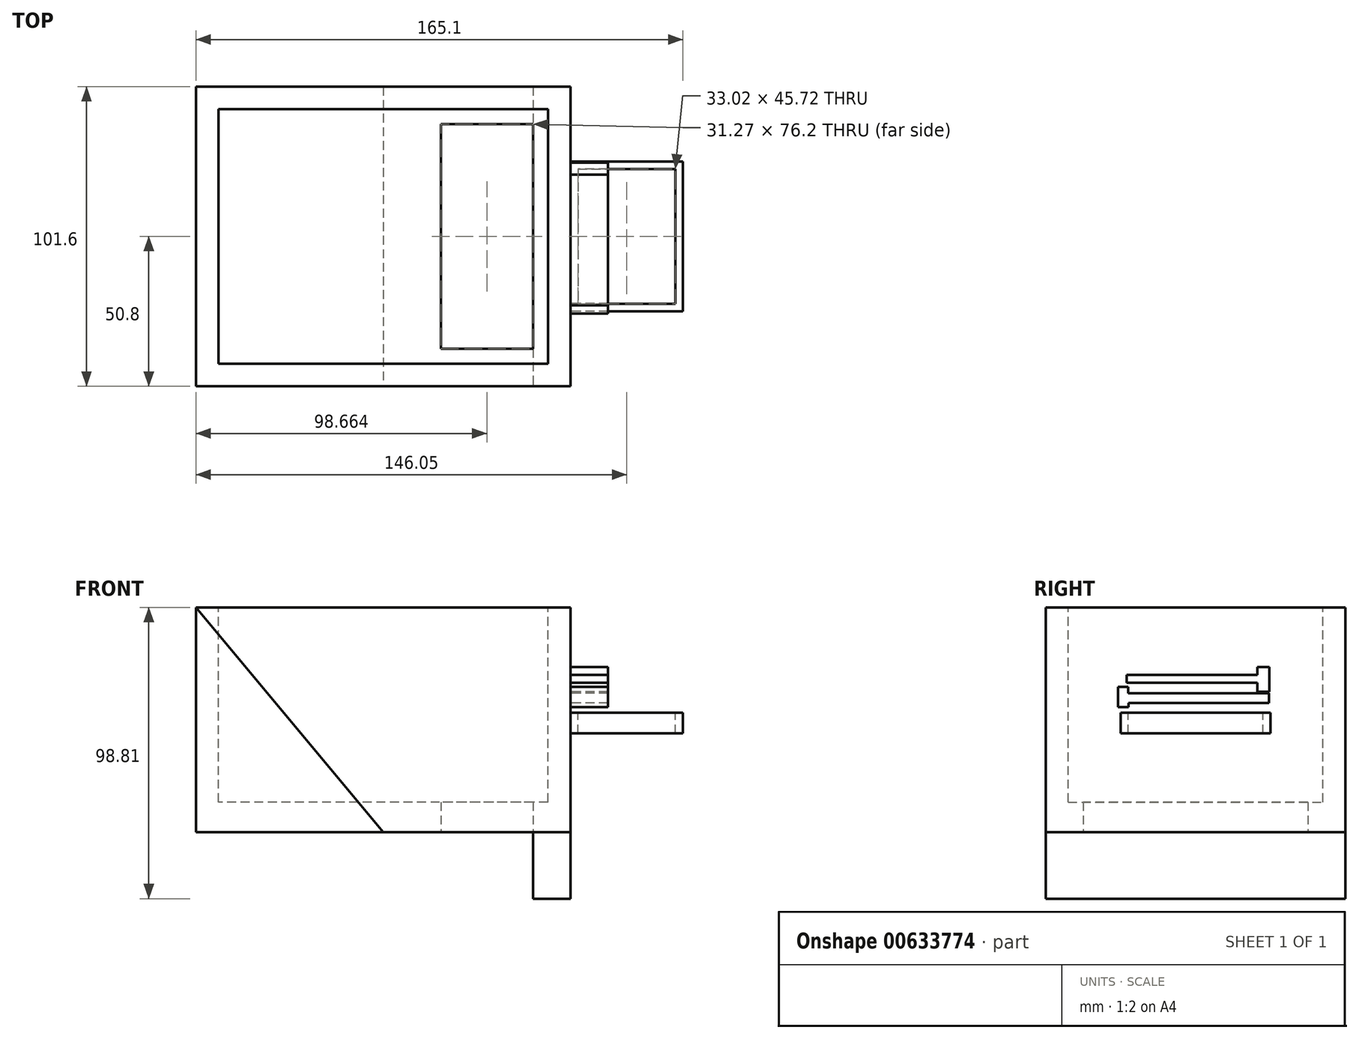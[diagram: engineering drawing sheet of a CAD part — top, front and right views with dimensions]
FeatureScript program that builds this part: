
annotation { "Feature Type Name" : "Feature", "Feature Type Description" : "" }
export const myFeature = defineFeature(function(context is Context, id is Id, definition is map)
    precondition{}
    {
        {
            var Q0;
            Q0=qCreatedBy(makeId("Front.planeOp"),FACE);
            var sketch = newSketch(context, id + "F0", { "sketchPlane" : qUnion([Q0])});
            skLineSegment(sketch, "E0", {"start": v(0, 0) * mm, "end": v(0, 76.2) * mm});
            skLineSegment(sketch, "E1", {"start": v(0, 76.2) * mm, "end": v(127, 76.2) * mm});
            skLineSegment(sketch, "E2", {"start": v(127, 76.2) * mm, "end": v(127, 0) * mm});
            skLineSegment(sketch, "E3", {"start": v(127, 0) * mm, "end": v(0, 0) * mm});
            skSolve(sketch);
        }
        {
            var Q0;
            Q0=makeQuery(id+"F0.imprint","IMPRINT",FACE,{"disambiguationData":[TD([[makeQuery(id+"F0.imprint","IMPRINT",EDGE,{"derivedFrom":sQuery(id+"F0.wireOp",EDGE,"E0")}),-1.0]])]});
            extrude(context, id + "F1", {"entities" : qUnion([Q0]), "oppositeDirection" : true, "depth" : 101.6 * mm, "offsetDistance" : 25.4 * mm});
        }
        {
            var Q0;
            Q0=makeQuery(id+"F1.opExtrude","SWEPT_FACE",FACE,{"disambiguationData":[OSD([sQuery(id+"F0.wireOp",EDGE,"E1")])]});
            var sketch = newSketch(context, id + "F2", { "sketchPlane" : qUnion([Q0])});
            skLineSegment(sketch, "E4", {"start": v(7.62, 7.62) * mm, "end": v(7.62, 93.98) * mm});
            skLineSegment(sketch, "E5", {"start": v(7.62, 93.98) * mm, "end": v(119.38, 93.98) * mm});
            skLineSegment(sketch, "E6", {"start": v(119.38, 93.98) * mm, "end": v(119.38, 7.62) * mm});
            skLineSegment(sketch, "E7", {"start": v(119.38, 7.62) * mm, "end": v(7.62, 7.62) * mm});
            skSolve(sketch);
        }
        {
            var Q0;
            Q0=makeQuery(id+"F2.imprint","IMPRINT",FACE,{"disambiguationData":[TD([[makeQuery(id+"F2.imprint","IMPRINT",EDGE,{"derivedFrom":sQuery(id+"F2.wireOp",EDGE,"E4")}),-1.0]])]});
            extrude(context, id + "F3", {"entities" : qUnion([Q0]), "operationType" : NewBodyOperationType.REMOVE, "oppositeDirection" : true, "depth" : 66.04 * mm, "offsetDistance" : 25.4 * mm});
        }
        {
            var Q0;
            Q0=makeQuery(id+"F1.opExtrude","SWEPT_FACE",FACE,{"disambiguationData":[OSD([sQuery(id+"F0.wireOp",EDGE,"E3")])]});
            var sketch = newSketch(context, id + "F4", { "sketchPlane" : qUnion([Q0])});
            skLineSegment(sketch, "E8", {"start": v(83.03, -12.7) * mm, "end": v(114.3, -12.7) * mm});
            skLineSegment(sketch, "E9", {"start": v(114.3, -12.7) * mm, "end": v(114.3, -88.9) * mm});
            skLineSegment(sketch, "E10", {"start": v(114.3, -88.9) * mm, "end": v(90.36, -88.9) * mm});
            skLineSegment(sketch, "E11", {"start": v(90.36, -88.9) * mm, "end": v(83.03, -88.9) * mm});
            skLineSegment(sketch, "E12", {"start": v(83.03, -88.9) * mm, "end": v(83.03, -12.7) * mm});
            skSolve(sketch);
        }
        {
            var Q0;
            Q0=makeQuery(id+"F4.imprint","IMPRINT",FACE,{"disambiguationData":[TD([[makeQuery(id+"F4.imprint","IMPRINT",EDGE,{"derivedFrom":sQuery(id+"F4.wireOp",EDGE,"E8")}),-1.0]])]});
            extrude(context, id + "F5", {"entities" : qUnion([Q0]), "operationType" : NewBodyOperationType.REMOVE, "oppositeDirection" : true, "depth" : 25.4 * mm, "offsetDistance" : 25.4 * mm});
        }
        {
            var Q0;
            Q0=makeQuery(id+"F1.opExtrude","SWEPT_FACE",FACE,{"disambiguationData":[OSD([sQuery(id+"F0.wireOp",EDGE,"E3")])]});
            var sketch = newSketch(context, id + "F6", { "sketchPlane" : qUnion([Q0])});
            skLineSegment(sketch, "E13", {"start": v(114.3, -12.7) * mm, "end": v(114.3, 0) * mm});
            skLineSegment(sketch, "E14", {"start": v(114.3, 0) * mm, "end": v(127, 0) * mm});
            skLineSegment(sketch, "E15", {"start": v(127, 0) * mm, "end": v(127, -101.6) * mm});
            skLineSegment(sketch, "E16", {"start": v(127, -101.6) * mm, "end": v(114.3, -101.6) * mm});
            skLineSegment(sketch, "E17", {"start": v(114.3, -101.6) * mm, "end": v(114.3, -88.9) * mm});
            skLineSegment(sketch, "E18", {"start": v(114.3, -88.9) * mm, "end": v(114.3, -12.7) * mm});
            skSolve(sketch);
        }
        {
            var Q0;
            Q0=makeQuery(id+"F6.imprint","IMPRINT",FACE,{"disambiguationData":[TD([[makeQuery(id+"F6.imprint","IMPRINT",EDGE,{"derivedFrom":sQuery(id+"F6.wireOp",EDGE,"E13")}),-1.0]])]});
            extrude(context, id + "F7", {"entities" : qUnion([Q0]), "depth" : 22.6 * mm, "offsetDistance" : 25.4 * mm});
        }
        {
            var Q0;
            Q0=makeQuery(id+"F7.boolean.opBoolean","MERGE",FACE,{"derivedFrom":[makeQuery(id+"F1.opExtrude","CAP_FACE",FACE,{"disambiguationData":[OSD([sQuery(id+"F0.wireOp",EDGE,"E0"),sQuery(id+"F0.wireOp",EDGE,"E1"),sQuery(id+"F0.wireOp",EDGE,"E2"),sQuery(id+"F0.wireOp",EDGE,"E3")])],"isStart":true}),makeQuery(id+"F7.opExtrude","SWEPT_FACE",FACE,{"disambiguationData":[OSD([sQuery(id+"F6.wireOp",EDGE,"E14")])]})]});
            var sketch = newSketch(context, id + "F8", { "sketchPlane" : qUnion([Q0])});
            skLineSegment(sketch, "E19", {"start": v(0, 76.2) * mm, "end": v(63.5, 0) * mm});
            skPoint(sketch, "E19.endSnap0", {"position": v(63.5, 76.2) * mm});
            skLineSegment(sketch, "E20", {"start": v(63.5, 0) * mm, "end": v(0, 0) * mm});
            skLineSegment(sketch, "E21", {"start": v(0, 0) * mm, "end": v(0, 76.2) * mm});
            skSolve(sketch);
        }
        {
            var Q0;
            Q0=makeQuery(id+"F8.imprint","IMPRINT",FACE,{"disambiguationData":[TD([[makeQuery(id+"F8.imprint","IMPRINT",EDGE,{"derivedFrom":sQuery(id+"F8.wireOp",EDGE,"E19")}),-1.0]])]});
            extrude(context, id + "F9", {"entities" : qUnion([Q0]), "oppositeDirection" : true, "depth" : 101.6 * mm, "offsetDistance" : 25.4 * mm});
        }
        {
            var Q0;
            Q0=makeQuery(id+"F7.boolean.opBoolean","MERGE",FACE,{"derivedFrom":[makeQuery(id+"F1.opExtrude","SWEPT_FACE",FACE,{"disambiguationData":[OSD([sQuery(id+"F0.wireOp",EDGE,"E2")])]}),makeQuery(id+"F7.opExtrude","SWEPT_FACE",FACE,{"disambiguationData":[OSD([sQuery(id+"F6.wireOp",EDGE,"E15")])]})]});
            var sketch = newSketch(context, id + "F10", { "sketchPlane" : qUnion([Q0])});
            skLineSegment(sketch, "E22", {"start": v(25.4, 33.43) * mm, "end": v(25.4, 40.49) * mm});
            skLineSegment(sketch, "E23", {"start": v(25.4, 40.49) * mm, "end": v(76.2, 40.49) * mm});
            skLineSegment(sketch, "E24", {"start": v(76.2, 40.49) * mm, "end": v(76.2, 33.43) * mm});
            skLineSegment(sketch, "E25", {"start": v(76.2, 33.43) * mm, "end": v(25.4, 33.43) * mm});
            skSolve(sketch);
        }
        {
            var Q0;
            Q0=makeQuery(id+"F10.imprint","IMPRINT",FACE,{"disambiguationData":[TD([[makeQuery(id+"F10.imprint","IMPRINT",EDGE,{"derivedFrom":sQuery(id+"F10.wireOp",EDGE,"E22")}),-1.0]])]});
            extrude(context, id + "F11", {"entities" : qUnion([Q0]), "depth" : 38.1 * mm, "offsetDistance" : 25.4 * mm});
        }
        {
            var Q0;
            Q0=makeQuery(id+"F11.opExtrude","SWEPT_FACE",FACE,{"disambiguationData":[OSD([sQuery(id+"F10.wireOp",EDGE,"E23")])]});
            var sketch = newSketch(context, id + "F12", { "sketchPlane" : qUnion([Q0])});
            skLineSegment(sketch, "E26", {"start": v(129.62, 31.75) * mm, "end": v(161.04, 31.75) * mm});
            skLineSegment(sketch, "E27", {"start": v(161.04, 31.75) * mm, "end": v(161.04, 69.85) * mm});
            skLineSegment(sketch, "E28", {"start": v(161.04, 69.85) * mm, "end": v(129.62, 69.85) * mm});
            skLineSegment(sketch, "E29", {"start": v(129.62, 69.85) * mm, "end": v(129.62, 31.75) * mm});
            skSolve(sketch);
        }
        {
            var Q0;
            Q0=makeQuery(id+"F12.imprint","IMPRINT",FACE,{"disambiguationData":[TD([[makeQuery(id+"F12.imprint","IMPRINT",EDGE,{"derivedFrom":sQuery(id+"F12.wireOp",EDGE,"E26")}),1.0]])]});
            extrude(context, id + "F13", {"entities" : qUnion([Q0]), "operationType" : NewBodyOperationType.REMOVE, "oppositeDirection" : true, "depth" : 50.8 * mm, "offsetDistance" : 25.4 * mm});
        }
        {
            var Q0;
            Q0=makeQuery(id+"F11.opExtrude","CAP_FACE",FACE,{"disambiguationData":[OSD([sQuery(id+"F10.wireOp",EDGE,"E22"),sQuery(id+"F10.wireOp",EDGE,"E23"),sQuery(id+"F10.wireOp",EDGE,"E24"),sQuery(id+"F10.wireOp",EDGE,"E25")])],"isStart":false});
            var sketch = newSketch(context, id + "F14", { "sketchPlane" : qUnion([Q0])});
            skCircle(sketch, "E30", {"center": v(49.91, 37.47) * mm, "radius": 3.25 * mm});
            skSolve(sketch);
        }
        {
            var Q0;
            {var subQ0=sQuery(id+"F14.wireOp",EDGE,"E30");var subQ1=makeQuery(id+"F11.opExtrude","CAP_EDGE",EDGE,{"disambiguationData":[OSD([sQuery(id+"F10.wireOp",EDGE,"E23")])],"isStart":false});var subQ2=makeQuery(id+"F14.imprint","INTERSECT",VERTEX,{"disambiguationData":[OD(0.0)],"derivedFrom":[subQ1,subQ0]});Q0=makeQuery(id+"F14.imprint","IMPRINT",FACE,{"disambiguationData":[TD([[makeQuery(id+"F14.imprint","IMPRINT",EDGE,{"disambiguationData":[TD([[subQ2,-1.0]])],"derivedFrom":subQ0}),1.0]])]});}
            var Q1;
            Q1=sQuery(id+"F14.wireOp",EDGE,"E30");
            extrude(context, id + "F15", {"entities" : qUnion([Q0]), "bodyType" : ToolBodyType.SURFACE, "surfaceEntities" : qUnion([Q1]), "depth" : 76.2 * mm, "offsetDistance" : 25.4 * mm});
        }
        {
            var Q0;
            Q0=makeQuery(id+"F11.opExtrude","SWEPT_FACE",FACE,{"disambiguationData":[OSD([sQuery(id+"F10.wireOp",EDGE,"E23")])]});
            var sketch = newSketch(context, id + "F16", { "sketchPlane" : qUnion([Q0])});
            skLineSegment(sketch, "E31", {"start": v(129.54, 27.94) * mm, "end": v(129.54, 73.66) * mm});
            skLineSegment(sketch, "E32", {"start": v(129.54, 73.66) * mm, "end": v(162.56, 73.66) * mm});
            skLineSegment(sketch, "E33", {"start": v(162.56, 73.66) * mm, "end": v(162.56, 27.94) * mm});
            skLineSegment(sketch, "E34", {"start": v(162.56, 27.94) * mm, "end": v(129.54, 27.94) * mm});
            skSolve(sketch);
        }
        {
            var Q0;
            Q0=makeQuery(id+"F16.imprint","IMPRINT",FACE,{"disambiguationData":[TD([[makeQuery(id+"F16.imprint","IMPRINT",EDGE,{"derivedFrom":sQuery(id+"F16.wireOp",EDGE,"E31")}),-1.0]])]});
            extrude(context, id + "F17", {"entities" : qUnion([Q0]), "operationType" : NewBodyOperationType.REMOVE, "oppositeDirection" : true, "depth" : 25.4 * mm, "offsetDistance" : 25.4 * mm});
        }
        {
            var Q0;
            Q0=makeQuery(id+"F1.opExtrude","SWEPT_FACE",FACE,{"disambiguationData":[OSD([sQuery(id+"F0.wireOp",EDGE,"E2")])]});
            var sketch = newSketch(context, id + "F18", { "sketchPlane" : qUnion([Q0])});
            skLineSegment(sketch, "E35", {"start": v(24.59, 42.33) * mm, "end": v(24.59, 49.27) * mm});
            skLineSegment(sketch, "E36", {"start": v(24.59, 49.27) * mm, "end": v(28, 49.27) * mm});
            skLineSegment(sketch, "E37", {"start": v(28, 49.27) * mm, "end": v(28, 47.03) * mm});
            skLineSegment(sketch, "E38", {"start": v(28, 47.03) * mm, "end": v(61.32, 47.03) * mm});
            skLineSegment(sketch, "E39", {"start": v(61.32, 47.03) * mm, "end": v(75.74, 47.03) * mm});
            skLineSegment(sketch, "E40", {"start": v(75.74, 47.03) * mm, "end": v(75.74, 43.72) * mm});
            skLineSegment(sketch, "E41", {"start": v(75.74, 43.72) * mm, "end": v(28.1, 43.72) * mm});
            skLineSegment(sketch, "E42", {"start": v(28.1, 43.72) * mm, "end": v(28.1, 42.33) * mm});
            skLineSegment(sketch, "E43", {"start": v(28.1, 42.33) * mm, "end": v(24.59, 42.33) * mm});
            skSolve(sketch);
        }
        {
            var Q0;
            Q0=makeQuery(id+"F18.imprint","IMPRINT",FACE,{"disambiguationData":[TD([[makeQuery(id+"F18.imprint","IMPRINT",EDGE,{"derivedFrom":sQuery(id+"F18.wireOp",EDGE,"E35")}),-1.0]])]});
            extrude(context, id + "F19", {"entities" : qUnion([Q0]), "operationType" : NewBodyOperationType.ADD, "depth" : 12.7 * mm, "offsetDistance" : 25.4 * mm});
        }
        {
            var Q0;
            Q0=makeQuery(id+"F1.opExtrude","SWEPT_FACE",FACE,{"disambiguationData":[OSD([sQuery(id+"F0.wireOp",EDGE,"E2")])]});
            var sketch = newSketch(context, id + "F20", { "sketchPlane" : qUnion([Q0])});
            skLineSegment(sketch, "E44", {"start": v(75.79, 48.75) * mm, "end": v(75.79, 52.47) * mm});
            skLineSegment(sketch, "E45", {"start": v(75.79, 52.47) * mm, "end": v(75.79, 55.91) * mm});
            skLineSegment(sketch, "E46", {"start": v(75.79, 55.91) * mm, "end": v(71.73, 55.91) * mm});
            skLineSegment(sketch, "E47", {"start": v(71.73, 55.91) * mm, "end": v(71.73, 53.35) * mm});
            skLineSegment(sketch, "E48", {"start": v(71.73, 53.35) * mm, "end": v(27.48, 53.35) * mm});
            skLineSegment(sketch, "E49", {"start": v(27.48, 53.35) * mm, "end": v(27.48, 50.65) * mm});
            skLineSegment(sketch, "E50", {"start": v(27.48, 50.65) * mm, "end": v(71.73, 50.65) * mm});
            skLineSegment(sketch, "E51", {"start": v(71.73, 50.65) * mm, "end": v(71.73, 47.6) * mm});
            skLineSegment(sketch, "E52", {"start": v(71.73, 47.6) * mm, "end": v(75.79, 47.6) * mm});
            skLineSegment(sketch, "E53", {"start": v(75.79, 47.6) * mm, "end": v(75.79, 48.75) * mm});
            skSolve(sketch);
        }
        {
            var Q0;
            Q0=makeQuery(id+"F20.imprint","IMPRINT",FACE,{"disambiguationData":[TD([[makeQuery(id+"F20.imprint","IMPRINT",EDGE,{"derivedFrom":sQuery(id+"F20.wireOp",EDGE,"E44")}),1.0]])]});
            extrude(context, id + "F21", {"entities" : qUnion([Q0]), "operationType" : NewBodyOperationType.ADD, "depth" : 12.7 * mm, "offsetDistance" : 25.4 * mm});
        }
    });
